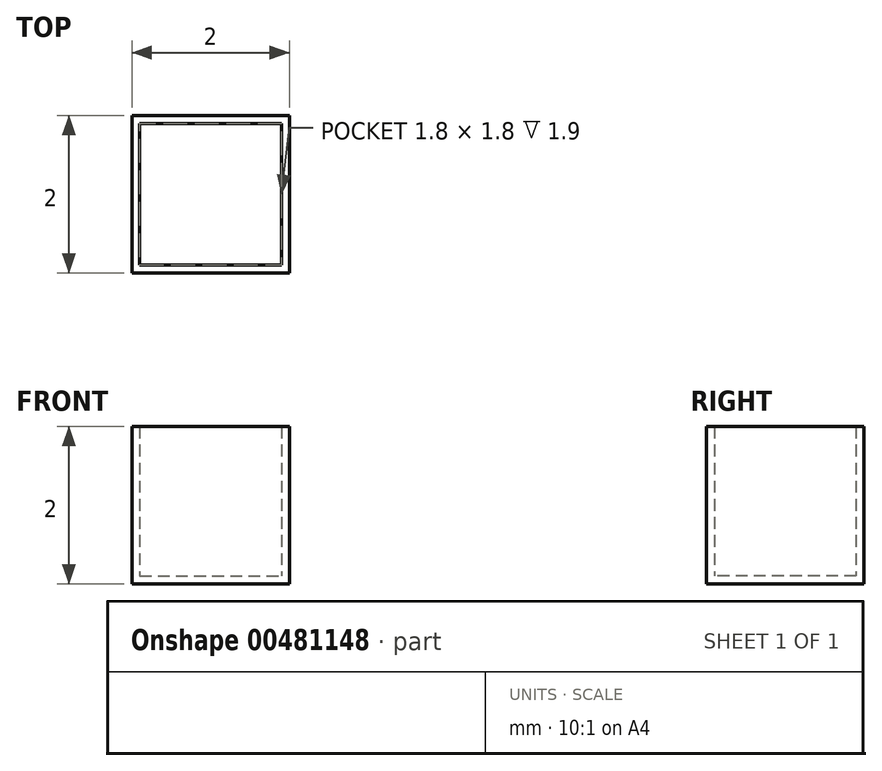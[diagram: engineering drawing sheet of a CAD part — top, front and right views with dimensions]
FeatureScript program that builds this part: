
annotation { "Feature Type Name" : "Feature", "Feature Type Description" : "" }
export const myFeature = defineFeature(function(context is Context, id is Id, definition is map)
    precondition{}
    {
        {
            assignVariable(context, id + "F0", {"name" : "height", "anyValue" : 2});
        }
        {
            var Q0;
            Q0=qCreatedBy(makeId("Top.planeOp"),FACE);
            var sketch = newSketch(context, id + "F1", { "sketchPlane" : qUnion([Q0])});
            skLineSegment(sketch, "E0.bottom", {"start": v(-1, 1) * mm, "end": v(1, 1) * mm});
            skLineSegment(sketch, "E0.top", {"start": v(-1, -1) * mm, "end": v(1, -1) * mm});
            skLineSegment(sketch, "E0.left", {"start": v(-1, 1) * mm, "end": v(-1, -1) * mm});
            skLineSegment(sketch, "E0.right", {"start": v(1, 1) * mm, "end": v(1, -1) * mm});
            skPoint(sketch, "E0.middle", {"position": v(0, 0) * mm});
            skSolve(sketch);
        }
        {
            var Q0;
            Q0 = qSketchRegion(id + "F1", true);
            extrude(context, id + "F2", {"entities" : qUnion([Q0]), "depth" : (getVariable(context, 'height')) * mm});
        }
        {
            var Q0;
            Q0=makeQuery(id+"F2.opExtrude","CAP_FACE",FACE,{"disambiguationData":[OSD([sQuery(id+"F1.wireOp",EDGE,"E0.bottom"),sQuery(id+"F1.wireOp",EDGE,"E0.top"),sQuery(id+"F1.wireOp",EDGE,"E0.left"),sQuery(id+"F1.wireOp",EDGE,"E0.right")])],"isStart":false});
            var Q1;
            Q1=makeQuery(id+"F2.opExtrude","SWEPT_BODY",BODY,{"disambiguationData":[OSD([sQuery(id+"F1.wireOp",EDGE,"E0.bottom"),sQuery(id+"F1.wireOp",EDGE,"E0.top"),sQuery(id+"F1.wireOp",EDGE,"E0.left"),sQuery(id+"F1.wireOp",EDGE,"E0.right")])]});
            shell(context, id + "F3", {"entities" : qUnion([Q0]), "parts" : qUnion([Q1]), "thickness" : 0.1 * mm});
        }
    });
